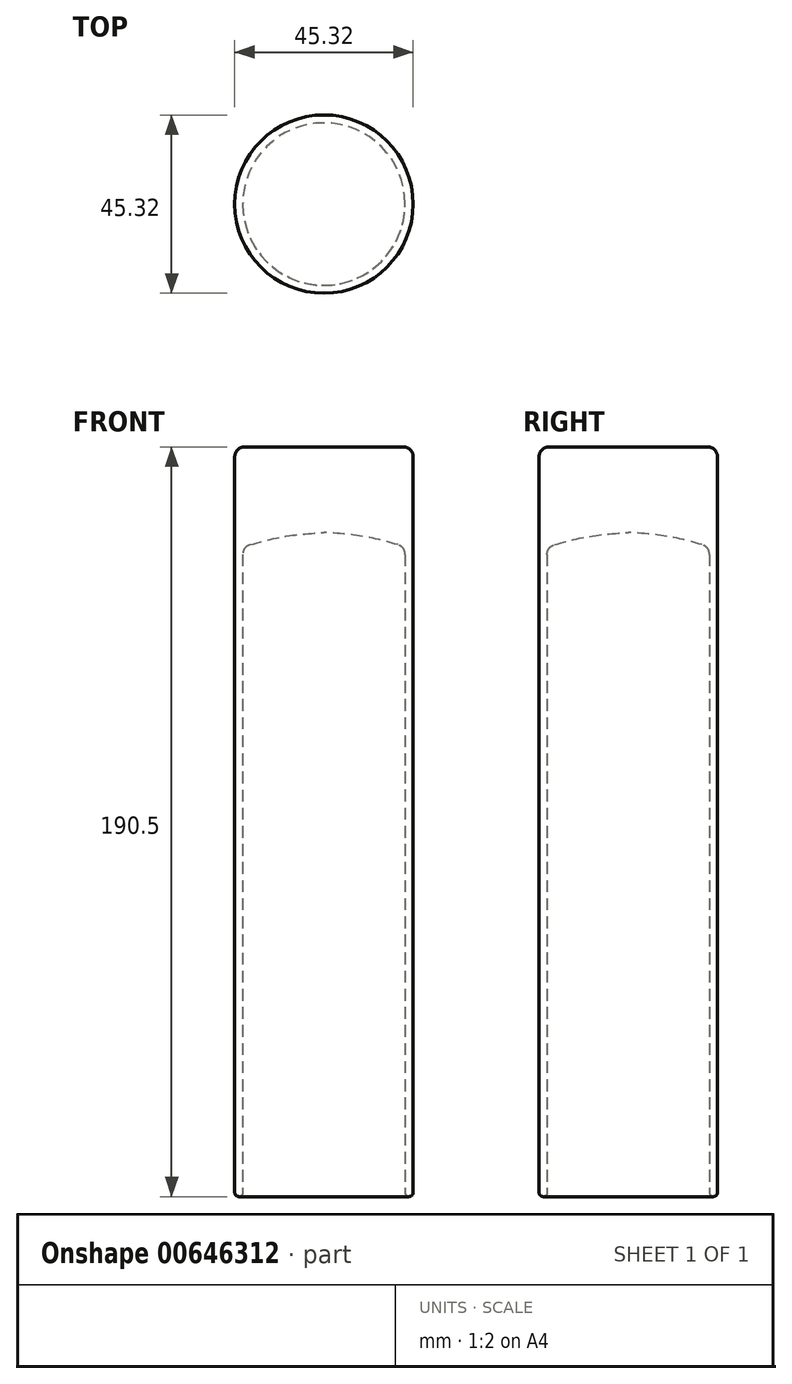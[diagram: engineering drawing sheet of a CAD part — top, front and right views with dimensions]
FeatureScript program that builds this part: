
annotation { "Feature Type Name" : "Feature", "Feature Type Description" : "" }
export const myFeature = defineFeature(function(context is Context, id is Id, definition is map)
    precondition{}
    {
        {
            var Q0;
            Q0=qCreatedBy(makeId("Front.planeOp"),FACE);
            var sketch = newSketch(context, id + "F0", { "sketchPlane" : qUnion([Q0])});
            skLineSegment(sketch, "E0", {"start": v(0, 0) * mm, "end": v(-22.66, 0) * mm});
            skLineSegment(sketch, "E1", {"start": v(-22.66, 0) * mm, "end": v(-22.66, -190.5) * mm});
            skLineSegment(sketch, "E2", {"start": v(-22.66, -190.5) * mm, "end": v(-20.62, -190.5) * mm});
            skLineSegment(sketch, "E3", {"start": v(-20.62, -190.5) * mm, "end": v(-20.62, -27.32) * mm});
            skFitSpline(sketch, "E4", {"points": [v(-20.62, -25.4) * mm, v(-9.75, -22.73) * mm, v(0, -21.8) * mm], "startDerivative": vector(21.27, 6.02) * mm, "endDerivative": vector(19.97, 1.14) * mm});
            skLineSegment(sketch, "E5", {"start": v(0, -21.8) * mm, "end": v(0, 0) * mm});
            skArc(sketch, "E6.filletArc", {"start": v(-18.77, -24.88) * mm, "mid": v(-20.1, -25.79) * mm, "end": v(-20.62, -27.32) * mm});
            skSolve(sketch);
        }
        {
            var Q0;
            Q0=makeQuery(id+"F0.imprint","IMPRINT",FACE,{"disambiguationData":[TD([[makeQuery(id+"F0.imprint","IMPRINT",EDGE,{"derivedFrom":sQuery(id+"F0.wireOp",EDGE,"E0")}),1.0]])]});
            var Q1;
            Q1=sQuery(id+"F0.wireOp",EDGE,"E5");
            revolve(context, id + "F1", {"entities" : qUnion([Q0]), "axis" : qUnion([Q1]), "revolveType" : RevolveType.FULL});
        }
        {
            var Q0;
            Q0=makeQuery(id+"F1.opRevolve","SWEPT_EDGE",EDGE,{"disambiguationData":[OSD([sQuery(id+"F0.wireOp",EDGE,"E0"),sQuery(id+"F0.wireOp",EDGE,"E1")])]});
            fillet(context, id + "F2", {"entities" : qUnion([Q0]), "radius" : 2.54 * mm, "tangentPropagation" : true, "allowEdgeOverflow" : false});
        }
        {
            var Q0;
            Q0=makeQuery(id+"F1.opRevolve","SWEPT_EDGE",EDGE,{"disambiguationData":[OSD([sQuery(id+"F0.wireOp",EDGE,"E1"),sQuery(id+"F0.wireOp",EDGE,"E2")])]});
            var Q1;
            Q1=makeQuery(id+"F1.opRevolve","SWEPT_EDGE",EDGE,{"disambiguationData":[OSD([sQuery(id+"F0.wireOp",EDGE,"E2"),sQuery(id+"F0.wireOp",EDGE,"E3")])]});
            fillet(context, id + "F3", {"entities" : qUnion([Q0, Q1]), "radius" : 1.02 * mm, "tangentPropagation" : true, "allowEdgeOverflow" : false});
        }
    });
